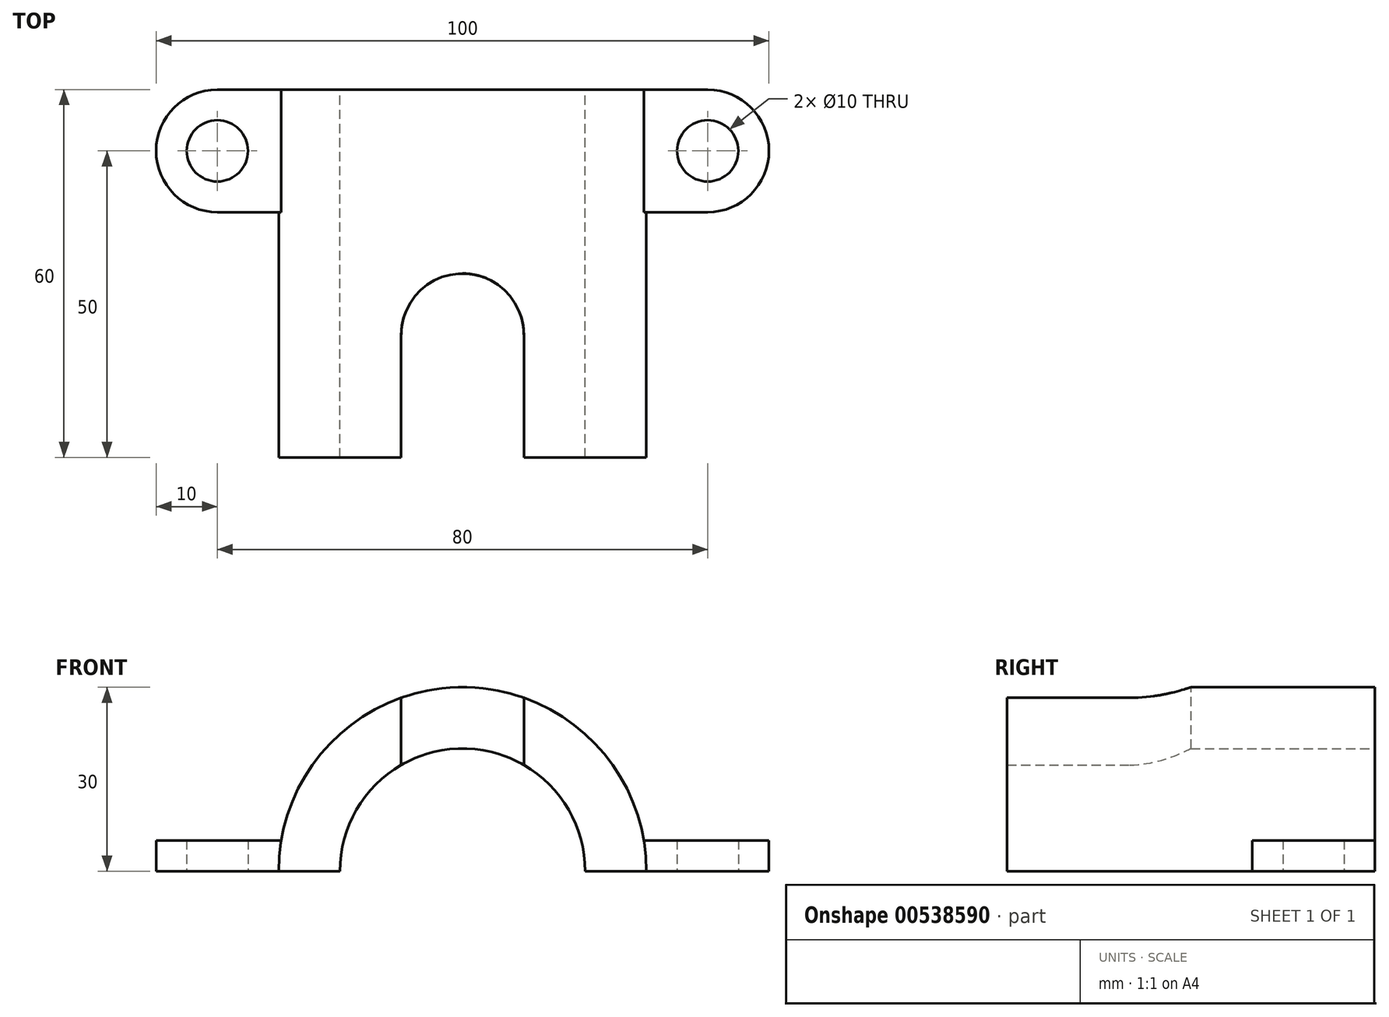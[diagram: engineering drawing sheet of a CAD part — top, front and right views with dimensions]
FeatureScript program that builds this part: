
annotation { "Feature Type Name" : "Feature", "Feature Type Description" : "" }
export const myFeature = defineFeature(function(context is Context, id is Id, definition is map)
    precondition{}
    {
        {
            assignVariable(context, id + "F0", {"name" : "A", "anyValue" : 5});
        }
        {
            var Q0;
            Q0=qCreatedBy(makeId("Front.planeOp"),FACE);
            var sketch = newSketch(context, id + "F1", { "sketchPlane" : qUnion([Q0])});
            skArc(sketch, "E0", {"start": v(-30, 0) * mm, "mid": v(0, 30) * mm, "end": v(30, 0) * mm});
            skLineSegment(sketch, "E1", {"start": v(-30, 0) * mm, "end": v(30, 0) * mm});
            skSolve(sketch);
        }
        {
            var Q0;
            Q0 = qSketchRegion(id + "F1", true);
            extrude(context, id + "F2", {"entities" : qUnion([Q0]), "depth" : 60 * mm, "offsetDistance" : 25 * mm});
        }
        {
            var Q0;
            Q0=qCreatedBy(makeId("Top.planeOp"),FACE);
            var sketch = newSketch(context, id + "F3", { "sketchPlane" : qUnion([Q0])});
            skLineSegment(sketch, "E2", {"start": v(-40, 0) * mm, "end": v(40, 0) * mm});
            skLineSegment(sketch, "E3", {"start": v(-80, -10) * mm, "end": v(90, -10) * mm, "construction": true});
            skLineSegment(sketch, "E4.MirrorCS", {"start": v(-40, -20) * mm, "end": v(40, -20) * mm});
            skArc(sketch, "E5", {"start": v(-40, 0) * mm, "mid": v(-50, -10) * mm, "end": v(-40, -20) * mm});
            skArc(sketch, "E6", {"start": v(40, -20) * mm, "mid": v(50, -10) * mm, "end": v(40, 0) * mm});
            skSolve(sketch);
        }
        {
            var Q0;
            Q0 = qSketchRegion(id + "F3", true);
            extrude(context, id + "F4", {"entities" : qUnion([Q0]), "operationType" : NewBodyOperationType.ADD, "depth" : (getVariable(context, 'A')) * mm, "offsetDistance" : 25 * mm});
        }
        {
            var Q0;
            Q0=qCreatedBy(makeId("Front.planeOp"),FACE);
            var sketch = newSketch(context, id + "F5", { "sketchPlane" : qUnion([Q0])});
            skArc(sketch, "E7", {"start": v(-20, 0) * mm, "mid": v(0, 20) * mm, "end": v(20, 0) * mm});
            skLineSegment(sketch, "E8", {"start": v(20, 0) * mm, "end": v(-20, 0) * mm});
            skSolve(sketch);
        }
        {
            var Q0;
            Q0 = qSketchRegion(id + "F5", true);
            extrude(context, id + "F6", {"entities" : qUnion([Q0]), "operationType" : NewBodyOperationType.REMOVE, "endBound" : BoundingType.THROUGH_ALL, "depth" : 25 * mm, "offsetDistance" : 25 * mm});
        }
        {
            var Q0;
            Q0=qCreatedBy(makeId("Top.planeOp"),FACE);
            cPlane(context, id + "F7", {"entities" : qUnion([Q0]), "cplaneType" : CPlaneType.OFFSET, "offset" : 30 * mm, "width" : 150 * mm, "height" : 150 * mm});
        }
        {
            var Q0;
            Q0=qCreatedBy(id+"F7.planeOp",FACE);
            var sketch = newSketch(context, id + "F8", { "sketchPlane" : qUnion([Q0])});
            skPoint(sketch, "E9", {"position": v(0, -60) * mm});
            skLineSegment(sketch, "E10", {"start": v(0, -60) * mm, "end": v(10, -60) * mm});
            skLineSegment(sketch, "E11", {"start": v(10, -60) * mm, "end": v(0, -60) * mm});
            skLineSegment(sketch, "E12", {"start": v(0, 0) * mm, "end": v(0, -65.4) * mm, "construction": true});
            skLineSegment(sketch, "E13.MirrorCS", {"start": v(-10, -60) * mm, "end": v(0, -60) * mm});
            skLineSegment(sketch, "E14", {"start": v(-10, -60) * mm, "end": v(-10, -40) * mm});
            skLineSegment(sketch, "E15.MirrorCS", {"start": v(10, -60) * mm, "end": v(10, -40) * mm});
            skArc(sketch, "E16", {"start": v(10, -40) * mm, "mid": v(0, -30) * mm, "end": v(-10, -40) * mm});
            skSolve(sketch);
        }
        {
            var Q0;
            Q0 = qSketchRegion(id + "F8", true);
            extrude(context, id + "F9", {"entities" : qUnion([Q0]), "operationType" : NewBodyOperationType.REMOVE, "endBound" : BoundingType.THROUGH_ALL, "oppositeDirection" : true, "depth" : 25 * mm, "offsetDistance" : 25 * mm});
        }
        {
            var Q0;
            Q0=qCreatedBy(makeId("Top.planeOp"),FACE);
            var sketch = newSketch(context, id + "F10", { "sketchPlane" : qUnion([Q0])});
            skLineSegment(sketch, "E17", {"start": v(0, 0) * mm, "end": v(0, -67.35) * mm, "construction": true});
            skCircle(sketch, "E18", {"center": v(-40, -10) * mm, "radius": 5 * mm});
            skCircle(sketch, "E19", {"center": v(40, -10) * mm, "radius": 5 * mm});
            skSolve(sketch);
        }
        {
            var Q0;
            Q0 = qSketchRegion(id + "F10", true);
            extrude(context, id + "F11", {"entities" : qUnion([Q0]), "operationType" : NewBodyOperationType.REMOVE, "endBound" : BoundingType.UP_TO_NEXT, "depth" : 25 * mm, "offsetDistance" : 25 * mm});
        }
    });
